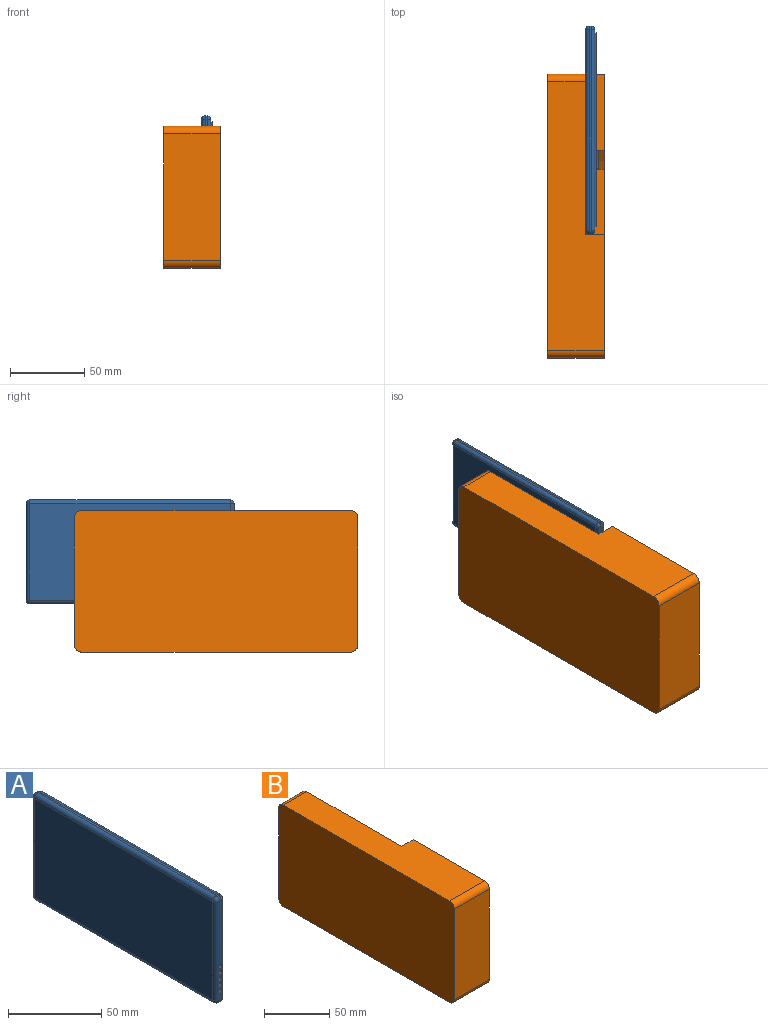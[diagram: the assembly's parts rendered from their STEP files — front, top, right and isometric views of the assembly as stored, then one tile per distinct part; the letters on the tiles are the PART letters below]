
ASSEMBLY  parts=2 mates=1
PART A: 59 faces, bbox 7.6x139.7x69.9 mm
  f0: plane 134.62x64.77mm, normal (1,0,0), area 955.4mm2, adj f24,f25,f34,f35,f41,f42,f43,f44
  f1: plane 1.27x1.27mm, normal (0,-1,0), area 1.1mm2, adj f17,f19,f34,f37
  f2: plane 1.45x1.27mm, normal (0,-1,0), area 1.4mm2, adj f15,f17,f34,f37
  f3: plane 1.27x1.18mm, normal (0,-1,0), area 1mm2, adj f13,f15,f34,f37
  f4: plane 1.37x1.27mm, normal (0,-1,0), area 1.3mm2, adj f11,f13,f34,f37
  f5: plane 4.34x1.27mm, normal (0,-1,0), area 5.3mm2, adj f11,f34,f37,f40
  f6: plane 41.62x1.27mm, normal (0,-1,0), area 52.6mm2, adj f19,f29,f34,f37
  f7: plane 134.62x1.27mm, normal (0,0,-1), area 171mm2, adj f26,f35,f36,f40
  f8: plane 64.77x1.27mm, normal (0,1,0), area 82.3mm2, adj f21,f25,f26,f27
  f9: plane 134.62x1.27mm, normal (0,0,1), area 171mm2, adj f21,f24,f28,f29
  f10: plane 134.62x64.77mm, normal (-1,0,0), area 8719.3mm2, adj f27,f28,f36,f37
  f11: cylinder r=1.59mm len=3.18mm, axis (0,-1,0), area 30.9mm2, adj f4,f5,f12,f34,f37
  f12: plane 3.18x3.18mm, normal (0,-1,0), area 7.9mm2, adj f11
  f13: cylinder r=1.59mm len=3.18mm, axis (0,-1,0), area 30.9mm2, adj f3,f4,f14,f34,f37
  f14: plane 3.18x3.18mm, normal (0,-1,0), area 7.9mm2, adj f13
  f15: cylinder r=1.59mm len=3.18mm, axis (0,-1,0), area 30.9mm2, adj f2,f3,f16,f34,f37
  f16: plane 3.18x3.18mm, normal (0,-1,0), area 7.9mm2, adj f15
  f17: cylinder r=1.59mm len=3.18mm, axis (0,-1,0), area 30.9mm2, adj f1,f2,f18,f34,f37
  f18: plane 3.18x3.18mm, normal (0,-1,0), area 7.9mm2, adj f17
  f19: cylinder r=1.59mm len=3.18mm, axis (0,-1,0), area 30.9mm2, adj f1,f6,f20,f34,f37
  f20: plane 3.18x3.18mm, normal (0,-1,0), area 7.9mm2, adj f19
  f21: cylinder r=2.54mm len=2.54mm, axis (1,0,0), area 5.1mm2, adj f8,f9,f22,f23
  f22: sphere r=2.54mm, area 10.1mm2, adj f21,f24,f25
  f23: sphere r=2.54mm, area 10.1mm2, adj f21,f27,f28
  f24: cylinder r=2.54mm len=134.62mm, axis (0,1,0), area 537.1mm2, adj f0,f9,f22,f30
  f25: cylinder r=2.54mm len=64.77mm, axis (0,0,-1), area 258.4mm2, adj f0,f8,f22,f31
  f26: cylinder r=2.54mm len=2.54mm, axis (-1,0,0), area 5.1mm2, adj f7,f8,f31,f32
  f27: cylinder r=2.54mm len=64.77mm, axis (0,0,1), area 258.4mm2, adj f8,f10,f23,f32
  f28: cylinder r=2.54mm len=134.62mm, axis (0,-1,0), area 537.1mm2, adj f9,f10,f23,f33
  f29: cylinder r=2.54mm len=2.54mm, axis (-1,0,0), area 5.1mm2, adj f6,f9,f30,f33
  f30: sphere r=2.54mm, area 10.1mm2, adj f24,f29,f34
  f31: sphere r=2.54mm, area 10.1mm2, adj f25,f26,f35
  f32: sphere r=2.54mm, area 10.1mm2, adj f26,f27,f36
  f33: sphere r=2.54mm, area 10.1mm2, adj f28,f29,f37
  f34: cylinder r=2.54mm len=64.77mm, axis (0,0,1), area 245.2mm2, adj f0,f1,f2,f3,f4,f5,f6,f11
  f35: cylinder r=2.54mm len=134.62mm, axis (0,-1,0), area 537.1mm2, adj f0,f7,f31,f38
  f36: cylinder r=2.54mm len=134.62mm, axis (0,1,0), area 537.1mm2, adj f7,f10,f32,f39
  f37: cylinder r=2.54mm len=64.77mm, axis (0,0,-1), area 251.1mm2, adj f1,f2,f3,f4,f5,f6,f10,f11
  f38: sphere r=2.54mm, area 10.1mm2, adj f34,f35,f40
  f39: sphere r=2.54mm, area 10.1mm2, adj f36,f37,f40
  f40: cylinder r=2.54mm len=2.54mm, axis (1,0,0), area 5.1mm2, adj f5,f7,f38,f39
  f41: plane 130.03x0.76mm, normal (0,0,-1), area 99.1mm2, adj f0,f42,f50,f54
  f42: plane 60.93x0.76mm, normal (0,1,0), area 46.4mm2, adj f0,f41,f43,f53
  f43: plane 130.03x0.76mm, normal (0,0,1), area 99.1mm2, adj f0,f42,f44,f55
  f44: plane 28.26x0.76mm, normal (0,-1,0), area 21.5mm2, adj f0,f43,f45,f57
  f45: cylinder r=7.18mm len=14.36mm, axis (-1,0,0), area 29.6mm2, adj f0,f44,f50,f58
  f46: cylinder r=1.42mm len=2.85mm, axis (-1,0,0), area 5.7mm2, adj f47,f49,f51,f52
  f47: plane 17.84x1.27mm, normal (0,-1,0), area 22.7mm2, adj f46,f48,f51,f52
  f48: cylinder r=1.42mm len=2.85mm, axis (-1,0,0), area 5.7mm2, adj f47,f49,f51,f52
  f49: plane 17.84x1.27mm, normal (0,1,0), area 22.7mm2, adj f46,f48,f51,f52
  f50: plane 26.59x0.76mm, normal (0,-1,0), area 20.3mm2, adj f0,f41,f45,f56
  f51: plane 129.01x59.92mm, normal (1,0,0), area 7498.4mm2, adj f46,f47,f48,f49,f53,f54,f55,f56
  f52: plane 20.69x2.85mm, normal (1,0,0), area 57.2mm2, adj f46,f47,f48,f49
  f53: cylinder r=0.51mm len=60.93mm, axis (0,0,-1), area 48.3mm2, adj f42,f51,f54,f55
  f54: cylinder r=0.51mm len=130.03mm, axis (0,-1,0), area 103.5mm2, adj f41,f51,f53,f56
  f55: cylinder r=0.51mm len=130.03mm, axis (0,1,0), area 103.5mm2, adj f43,f51,f53,f57
  f56: cylinder r=0.51mm len=26.59mm, axis (0,0,1), area 20.5mm2, adj f50,f51,f54,f58
  f57: cylinder r=0.51mm len=28.26mm, axis (0,0,1), area 21.8mm2, adj f44,f51,f55,f58
  f58: torus R=7.69mm, axis (1,0,0), area 30.6mm2, adj f45,f51,f56,f57
PART B: 39 faces, bbox 38.1x190.5x95.3 mm
  f0: plane 20.35x7.03mm, normal (1,0,0), area 21.1mm2, adj f15,f16,f33,f34
  f1: plane 53.08x16.6mm, normal (1,0,0), area 83.6mm2, adj f20,f27,f28,f29
  f2: plane 190.5x95.25mm, normal (1,0,0), area 7403.8mm2, adj f4,f5,f6,f7,f8,f10,f12,f13
  f3: plane 74.05x50.3mm, normal (1,0,0), area 974.3mm2, adj f4,f10,f12,f16,f17,f22,f23,f24
  f4: plane 107.95x12.7mm, normal (0,0,1), area 1295mm2, adj f2,f3,f8,f10,f11,f21,f22,f26
  f5: plane 180.34x38.1mm, normal (0,0,1), area 5564.5mm2, adj f2,f9,f10,f11,f37,f38
  f6: plane 85.09x38.1mm, normal (0,-1,0), area 3241.9mm2, adj f2,f9,f35,f38
  f7: plane 180.34x38.1mm, normal (0,0,-1), area 6871mm2, adj f2,f9,f35,f36
  f8: plane 85.09x38.1mm, normal (0,1,0), area 2500mm2, adj f2,f4,f9,f11,f36,f37
  f9: plane 190.5x95.25mm, normal (-1,0,0), area 18123mm2, adj f5,f6,f7,f8,f35,f36,f37,f38
  f10: plane 63.5x12.7mm, normal (0,1,0), area 724.8mm2, adj f2,f3,f4,f5,f11,f13,f18,f19
  f11: plane 107.95x63.5mm, normal (1,0,0), area 6849.3mm2, adj f4,f5,f8,f10,f37
  f12: sphere r=25.4mm, area 4053.7mm2, adj f2,f3,f15,f20
  f13: cylinder r=15.43mm len=3.81mm, axis (1,0,0), area 15.2mm2, adj f2,f10,f14,f32
  f14: cylinder r=31.53mm len=35.97mm, axis (1,0,0), area 171.1mm2, adj f2,f13,f15,f34
  f15: cylinder r=25.4mm len=7.86mm, axis (1,0,0), area 52.5mm2, adj f0,f12,f14,f16,f34
  f16: cylinder r=29.37mm len=6.35mm, axis (1,0,0), area 29.6mm2, adj f0,f3,f15,f17,f33
  f17: cylinder r=17.96mm len=18.13mm, axis (1,0,0), area 89.2mm2, adj f3,f16,f18,f31,f33
  f18: cylinder r=29.59mm len=22.93mm, axis (1,0,0), area 73.5mm2, adj f10,f17,f19,f31,f33
  f19: plane 25.53x10.12mm, normal (1,0,0), area 78.1mm2, adj f10,f18,f32,f33,f34
  f20: cylinder r=25.4mm len=6.5mm, axis (1,0,0), area 53.5mm2, adj f1,f12,f21,f25,f27,f28
  f21: cylinder r=71.43mm len=88.1mm, axis (1,0,0), area 361.9mm2, adj f2,f4,f20,f28
  f22: cylinder r=25.82mm len=16.53mm, axis (1,0,0), area 75.3mm2, adj f3,f4,f23,f30
  f23: cylinder r=111.68mm len=37.1mm, axis (1,0,0), area 142.3mm2, adj f3,f22,f24,f29
  f24: cylinder r=26.63mm len=14.06mm, axis (1,0,0), area 72.3mm2, adj f3,f23,f25,f27
  f25: cylinder r=26.33mm len=6.3mm, axis (1,0,0), area 12.4mm2, adj f3,f20,f24,f27
  f26: plane 12.95x7.76mm, normal (1,0,0), area 21.3mm2, adj f4,f28,f30
  f27: torus R=29.17mm, axis (1,0,0), area 77mm2, adj f1,f20,f24,f25,f29
  f28: torus R=68.89mm, axis (1,0,0), area 364.1mm2, adj f1,f4,f20,f21,f26,f29,f30
  f29: torus R=114.22mm, axis (1,0,0), area 150.2mm2, adj f1,f23,f27,f28,f30
  f30: torus R=28.36mm, axis (1,0,0), area 81mm2, adj f4,f22,f26,f28,f29
  f31: torus R=32.13mm, axis (1,0,0), area 90.7mm2, adj f3,f10,f17,f18
  f32: torus R=17.97mm, axis (1,0,0), area 22mm2, adj f10,f13,f19,f34
  f33: torus R=20.5mm, axis (1,0,0), area 94.2mm2, adj f0,f16,f17,f18,f19,f34
  f34: torus R=28.99mm, axis (1,0,0), area 167.2mm2, adj f0,f14,f15,f19,f32,f33
  f35: cylinder r=5.08mm len=38.1mm, axis (1,0,0), area 304mm2, adj f2,f6,f7,f9
  f36: cylinder r=5.08mm len=38.1mm, axis (-1,0,0), area 304mm2, adj f2,f7,f8,f9
  f37: cylinder r=5.08mm len=25.4mm, axis (1,0,0), area 202.7mm2, adj f5,f8,f9,f11
  f38: cylinder r=5.08mm len=38.1mm, axis (-1,0,0), area 304mm2, adj f2,f5,f6,f9
PLACE A t=(22.14,-46.38,12.94)mm
PLACE B t=(-3.26,-129.52,-19.42)mm
MATE fastened A.f10 <-> B.f11  axis (-1,0,0) through (22.14,23.47,47.86)mm
